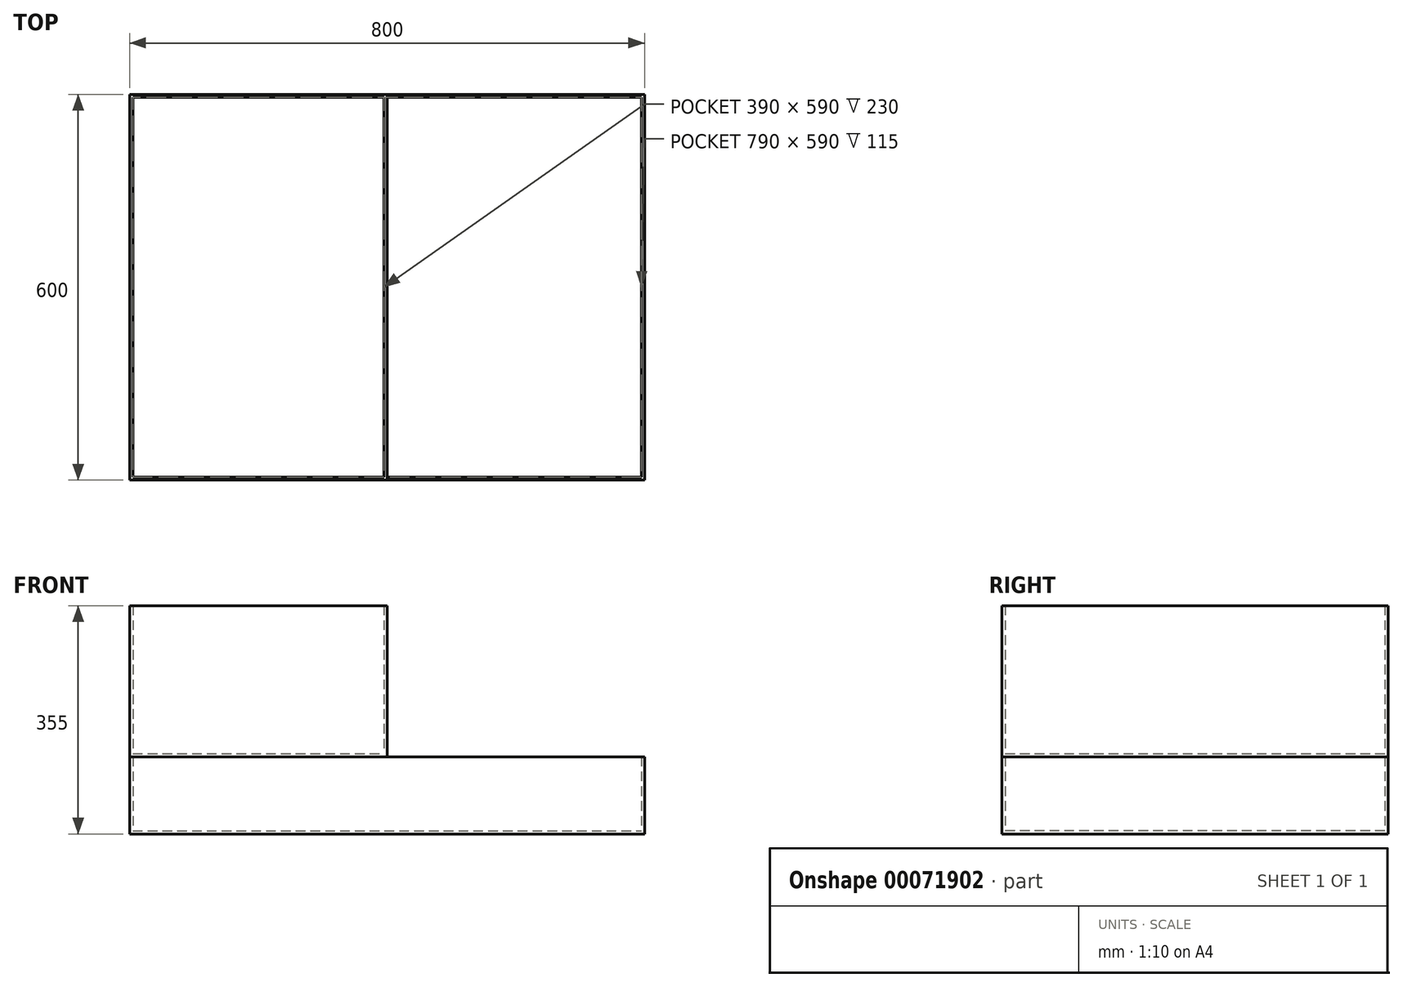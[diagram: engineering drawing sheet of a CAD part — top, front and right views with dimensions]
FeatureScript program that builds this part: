
annotation { "Feature Type Name" : "Feature", "Feature Type Description" : "" }
export const myFeature = defineFeature(function(context is Context, id is Id, definition is map)
    precondition{}
    {
        {
            var Q0;
            Q0=qCreatedBy(makeId("Top.planeOp"),FACE);
            var sketch = newSketch(context, id + "F0", { "sketchPlane" : qUnion([Q0])});
            skLineSegment(sketch, "E0.bottom", {"start": v(-400, 300) * mm, "end": v(400, 300) * mm});
            skLineSegment(sketch, "E0.top", {"start": v(-400, -300) * mm, "end": v(400, -300) * mm});
            skLineSegment(sketch, "E0.left", {"start": v(-400, 300) * mm, "end": v(-400, -300) * mm});
            skLineSegment(sketch, "E0.right", {"start": v(400, 300) * mm, "end": v(400, -300) * mm});
            skPoint(sketch, "E0.middle", {"position": v(0, 0) * mm});
            skSolve(sketch);
        }
        {
            var Q0;
            Q0 = qSketchRegion(id + "F0", true);
            extrude(context, id + "F1", {"entities" : qUnion([Q0]), "depth" : 120 * mm});
        }
        {
            var Q0;
            Q0=makeQuery(id+"F1.opExtrude","CAP_FACE",FACE,{"disambiguationData":[OSD([sQuery(id+"F0.wireOp",EDGE,"E0.bottom"),sQuery(id+"F0.wireOp",EDGE,"E0.top"),sQuery(id+"F0.wireOp",EDGE,"E0.left"),sQuery(id+"F0.wireOp",EDGE,"E0.right")])],"isStart":false});
            shell(context, id + "F2", {"entities" : qUnion([Q0]), "thickness" : 5 * mm});
        }
        {
            var Q0;
            Q0=makeQuery(id+"F1.opExtrude","CAP_FACE",FACE,{"disambiguationData":[OSD([sQuery(id+"F0.wireOp",EDGE,"E0.bottom"),sQuery(id+"F0.wireOp",EDGE,"E0.top"),sQuery(id+"F0.wireOp",EDGE,"E0.left"),sQuery(id+"F0.wireOp",EDGE,"E0.right")])],"isStart":false});
            var sketch = newSketch(context, id + "F3", { "sketchPlane" : qUnion([Q0])});
            skLineSegment(sketch, "E1.bottom", {"start": v(-400, -300) * mm, "end": v(0, -300) * mm});
            skLineSegment(sketch, "E1.top", {"start": v(-400, 300) * mm, "end": v(0, 300) * mm});
            skLineSegment(sketch, "E1.left", {"start": v(-400, -300) * mm, "end": v(-400, 300) * mm});
            skLineSegment(sketch, "E1.right", {"start": v(0, -300) * mm, "end": v(0, 300) * mm});
            skSolve(sketch);
        }
        {
            var Q0;
            Q0 = qSketchRegion(id + "F3", true);
            extrude(context, id + "F4", {"entities" : qUnion([Q0]), "depth" : 235 * mm});
        }
        {
            var Q0;
            Q0=makeQuery(id+"F4.opExtrude","CAP_FACE",FACE,{"disambiguationData":[OSD([sQuery(id+"F3.wireOp",EDGE,"E1.bottom"),sQuery(id+"F3.wireOp",EDGE,"E1.top"),sQuery(id+"F3.wireOp",EDGE,"E1.left"),sQuery(id+"F3.wireOp",EDGE,"E1.right")])],"isStart":false});
            shell(context, id + "F5", {"entities" : qUnion([Q0]), "thickness" : 5 * mm});
        }
    });
